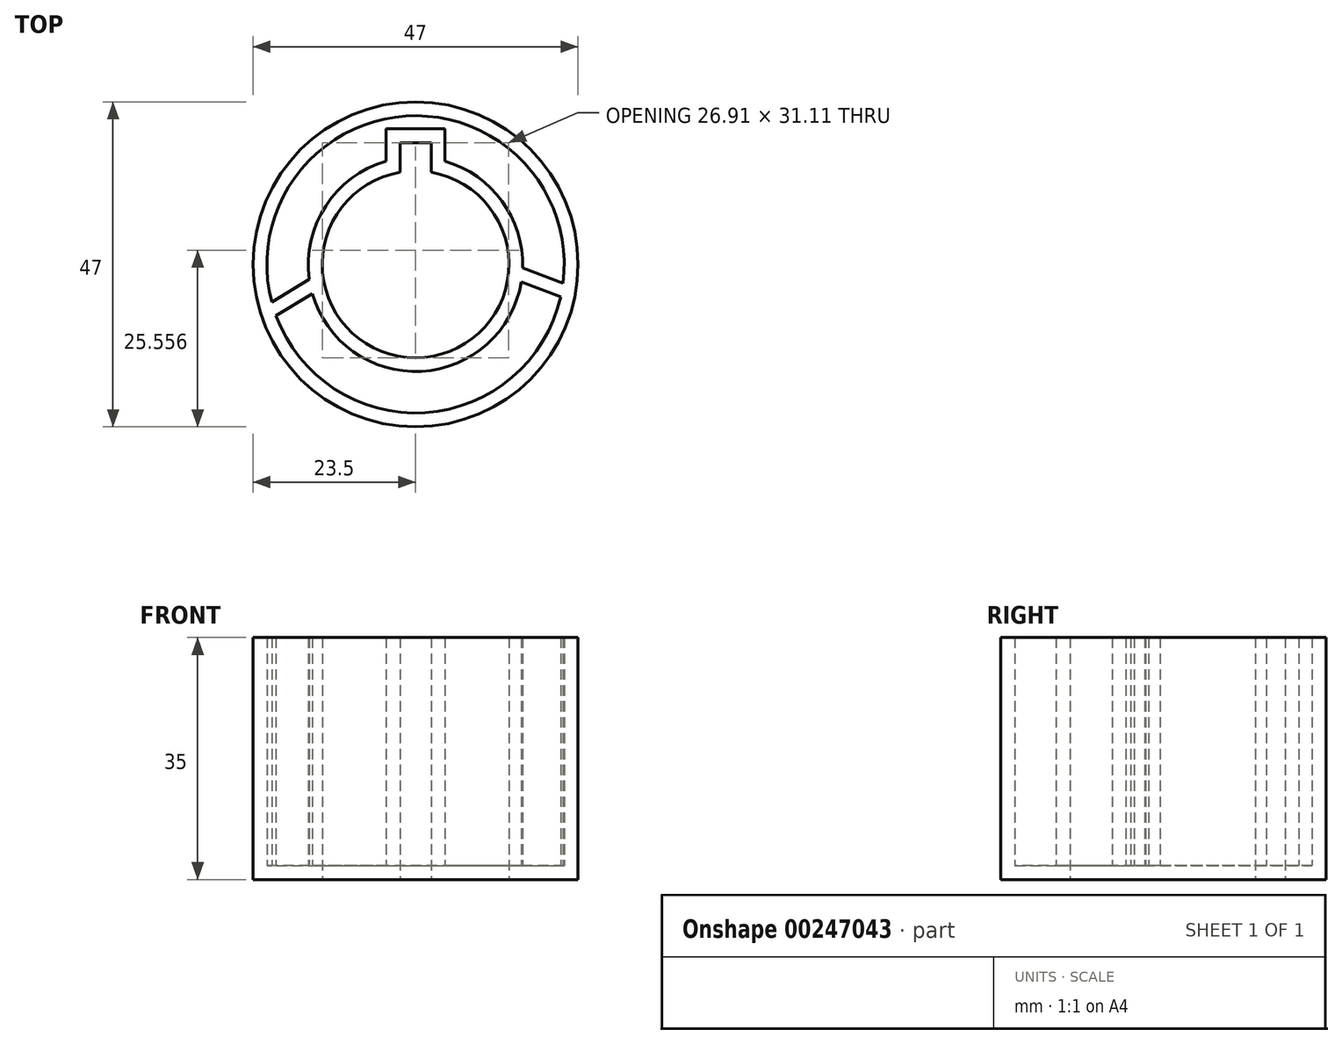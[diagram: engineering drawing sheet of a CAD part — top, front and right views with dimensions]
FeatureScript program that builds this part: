
annotation { "Feature Type Name" : "Feature", "Feature Type Description" : "" }
export const myFeature = defineFeature(function(context is Context, id is Id, definition is map)
    precondition{}
    {
        {
            var Q0;
            Q0=qCreatedBy(makeId("Top.planeOp"),FACE);
            var sketch = newSketch(context, id + "F0", { "sketchPlane" : qUnion([Q0])});
            skLineSegment(sketch, "E0.bottom", {"start": v(-2.25, 17.61) * mm, "end": v(2.25, 17.61) * mm});
            skLineSegment(sketch, "E0.left", {"start": v(-2.25, 17.61) * mm, "end": v(-2.25, 13.31) * mm});
            skLineSegment(sketch, "E0.right", {"start": v(2.25, 17.61) * mm, "end": v(2.25, 13.31) * mm});
            skCircle(sketch, "E1", {"center": v(0, 0) * mm, "radius": 23.5 * mm});
            skArc(sketch, "E2", {"start": v(-2.25, 13.31) * mm, "mid": v(0, -13.5) * mm, "end": v(2.25, 13.31) * mm});
            skLineSegment(sketch, "E3", {"start": v(13.37, -1.83) * mm, "end": v(22.86, -5.44) * mm});
            skLineSegment(sketch, "E4", {"start": v(-13.13, -3.15) * mm, "end": v(-21.93, -8.45) * mm});
            skPoint(sketch, "E5.startSnap0", {"position": v(-17.53, -5.8) * mm});
            skSolve(sketch);
        }
        {
            var Q0;
            Q0=makeQuery(id+"F0.imprint","IMPRINT",FACE,{"disambiguationData":[TD([[makeQuery(id+"F0.imprint","IMPRINT",EDGE,{"derivedFrom":sQuery(id+"F0.wireOp",EDGE,"E0.bottom")}),1.0]])]});
            extrude(context, id + "F1", {"entities" : qUnion([Q0]), "depth" : 35 * mm});
        }
        {
            var Q0;
            Q0=makeQuery(id+"F1.opExtrude","CAP_FACE",FACE,{"disambiguationData":[OSD([sQuery(id+"F0.wireOp",EDGE,"E0.bottom"),sQuery(id+"F0.wireOp",EDGE,"E0.left"),sQuery(id+"F0.wireOp",EDGE,"E0.right"),sQuery(id+"F0.wireOp",EDGE,"E1"),sQuery(id+"F0.wireOp",EDGE,"E2")])],"isStart":false});
            shell(context, id + "F2", {"entities" : qUnion([Q0]), "thickness" : 2 * mm});
        }
        {
            var Q0;
            {var subQ0=sQuery(id+"F0.wireOp",EDGE,"E3");Q0=makeQuery(id+"F0.imprint","IMPRINT",FACE,{"disambiguationData":[TD([[makeQuery(id+"F0.imprint","IMPRINT",EDGE,{"derivedFrom":subQ0}),-1.0]])]});}
            extrude(context, id + "F3", {"entities" : qUnion([Q0]), "operationType" : NewBodyOperationType.ADD, "depth" : 35 * mm});
        }
        {
            var Q0;
            {var subQ0=sQuery(id+"F0.wireOp",EDGE,"E4");var subQ1=sQuery(id+"F0.wireOp",EDGE,"E3");var subQ2=sQuery(id+"F0.wireOp",EDGE,"E2");var subQ3=sQuery(id+"F0.wireOp",EDGE,"E1");Q0=makeQuery(id+"F3.boolean.opBoolean","MERGE",FACE,{"derivedFrom":[makeQuery(id+"F1.opExtrude","CAP_FACE",FACE,{"disambiguationData":[OSD([sQuery(id+"F0.wireOp",EDGE,"E0.bottom"),sQuery(id+"F0.wireOp",EDGE,"E0.left"),sQuery(id+"F0.wireOp",EDGE,"E0.right"),subQ3,subQ2,subQ1,subQ0])],"isStart":false}),makeQuery(id+"F3.opExtrude","CAP_FACE",FACE,{"disambiguationData":[OSD([subQ3,subQ2,subQ1,subQ0])],"isStart":false})]});}
            shell(context, id + "F4", {"entities" : qUnion([Q0]), "thickness" : 2 * mm});
        }
    });
